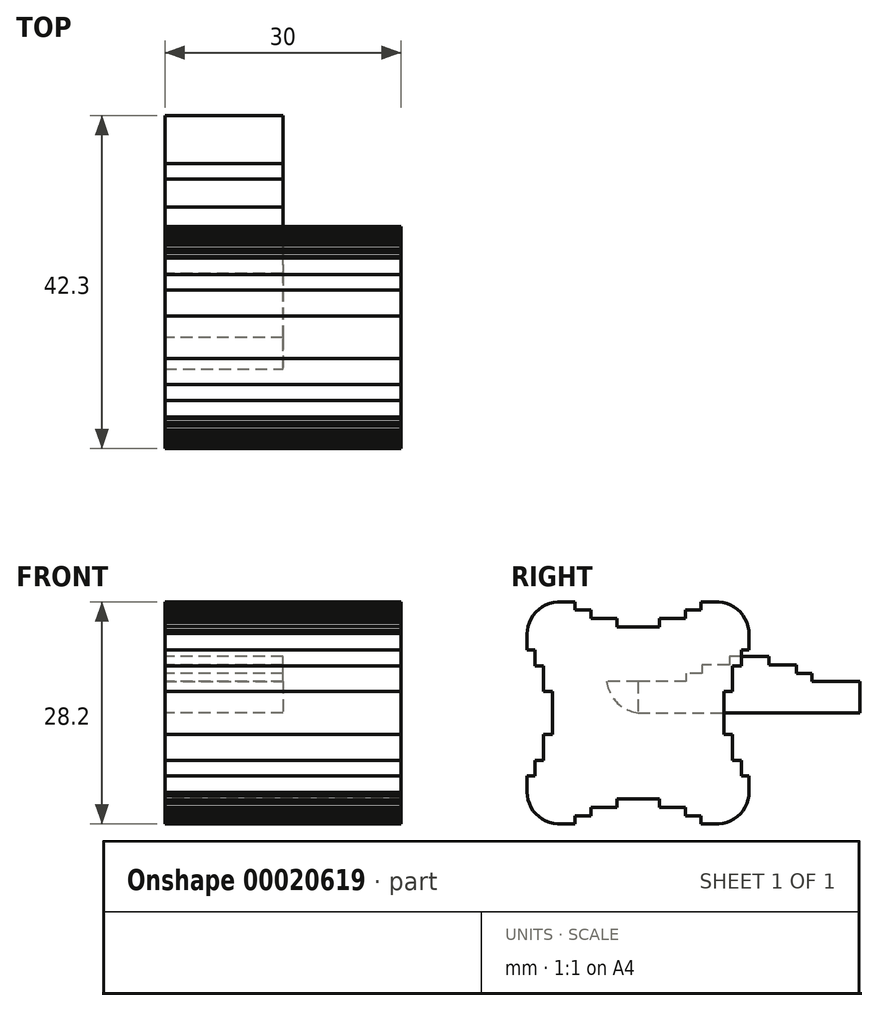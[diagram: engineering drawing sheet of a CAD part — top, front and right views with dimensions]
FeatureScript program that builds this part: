
annotation { "Feature Type Name" : "Feature", "Feature Type Description" : "" }
export const myFeature = defineFeature(function(context is Context, id is Id, definition is map)
    precondition{}
    {
        {
            var Q0;
            Q0=qCreatedBy(makeId("Right.planeOp"),FACE);
            var sketch = newSketch(context, id + "F0", { "sketchPlane" : qUnion([Q0])});
            skLineSegment(sketch, "E0", {"start": v(0, 0) * mm, "end": v(28.2, 0) * mm});
            skLineSegment(sketch, "E1", {"start": v(28.2, 0) * mm, "end": v(28.2, 4) * mm});
            skLineSegment(sketch, "E2", {"start": v(28.2, 4) * mm, "end": v(22.1, 4) * mm});
            skLineSegment(sketch, "E3", {"start": v(22.1, 4) * mm, "end": v(22.1, 5) * mm});
            skLineSegment(sketch, "E4", {"start": v(22.1, 5) * mm, "end": v(20.1, 5) * mm});
            skLineSegment(sketch, "E5", {"start": v(20.1, 5) * mm, "end": v(20.1, 6.1) * mm});
            skLineSegment(sketch, "E6", {"start": v(20.1, 6.1) * mm, "end": v(16.6, 6.1) * mm});
            skLineSegment(sketch, "E7", {"start": v(16.6, 6.1) * mm, "end": v(16.6, 7.2) * mm});
            skLineSegment(sketch, "E8", {"start": v(16.6, 7.2) * mm, "end": v(11.6, 7.2) * mm});
            skLineSegment(sketch, "E9", {"start": v(11.6, 7.2) * mm, "end": v(11.6, 6.1) * mm});
            skLineSegment(sketch, "E10", {"start": v(11.6, 6.1) * mm, "end": v(8.1, 6.1) * mm});
            skLineSegment(sketch, "E11", {"start": v(8.1, 6.1) * mm, "end": v(8.1, 5) * mm});
            skLineSegment(sketch, "E12", {"start": v(8.1, 5) * mm, "end": v(6.1, 5) * mm});
            skLineSegment(sketch, "E13", {"start": v(6.1, 5) * mm, "end": v(6.1, 4) * mm});
            skLineSegment(sketch, "E14", {"start": v(6.1, 4) * mm, "end": v(0, 4) * mm});
            skLineSegment(sketch, "E15", {"start": v(0, 4) * mm, "end": v(0, 0) * mm});
            skSolve(sketch);
        }
        {
            var Q0;
            Q0=qCreatedBy(makeId("Right.planeOp"),FACE);
            var sketch = newSketch(context, id + "F1", { "sketchPlane" : qUnion([Q0])});
            skLineSegment(sketch, "E16", {"start": v(-8, -13.1) * mm, "end": v(-6, -13.1) * mm});
            skLineSegment(sketch, "E17", {"start": v(-6, -13.1) * mm, "end": v(-6, -12) * mm});
            skLineSegment(sketch, "E18", {"start": v(-6, -12) * mm, "end": v(-2.7, -12) * mm});
            skLineSegment(sketch, "E19", {"start": v(-2.7, -12) * mm, "end": v(-2.7, -10.9) * mm});
            skLineSegment(sketch, "E20", {"start": v(-2.7, -10.9) * mm, "end": v(2.7, -10.9) * mm});
            skLineSegment(sketch, "E21", {"start": v(2.7, -10.9) * mm, "end": v(2.7, -12) * mm});
            skLineSegment(sketch, "E22", {"start": v(2.7, -12) * mm, "end": v(6, -12) * mm});
            skLineSegment(sketch, "E23", {"start": v(6, -12) * mm, "end": v(6, -13.1) * mm});
            skLineSegment(sketch, "E24", {"start": v(6, -13.1) * mm, "end": v(8, -13.1) * mm});
            skLineSegment(sketch, "E25", {"start": v(8, -13.1) * mm, "end": v(8, -14.1) * mm});
            skLineSegment(sketch, "E26", {"start": v(8, -14.1) * mm, "end": v(10.1, -14.1) * mm});
            skLineSegment(sketch, "E27", {"start": v(10.1, -14.1) * mm, "end": v(10.1, -14.1) * mm});
            skLineSegment(sketch, "E28", {"start": v(10.1, -14.1) * mm, "end": v(10.26, -14.1) * mm});
            skLineSegment(sketch, "E29", {"start": v(10.26, -14.1) * mm, "end": v(10.77, -14.03) * mm});
            skLineSegment(sketch, "E30", {"start": v(10.77, -14.03) * mm, "end": v(11.27, -13.9) * mm});
            skLineSegment(sketch, "E31", {"start": v(11.27, -13.9) * mm, "end": v(11.75, -13.7) * mm});
            skLineSegment(sketch, "E32", {"start": v(11.75, -13.7) * mm, "end": v(12.2, -13.46) * mm});
            skLineSegment(sketch, "E33", {"start": v(12.2, -13.46) * mm, "end": v(12.61, -13.16) * mm});
            skLineSegment(sketch, "E34", {"start": v(12.61, -13.16) * mm, "end": v(12.99, -12.8) * mm});
            skLineSegment(sketch, "E35", {"start": v(12.99, -12.8) * mm, "end": v(13.32, -12.4) * mm});
            skLineSegment(sketch, "E36", {"start": v(13.32, -12.4) * mm, "end": v(13.6, -11.98) * mm});
            skLineSegment(sketch, "E37", {"start": v(13.6, -11.98) * mm, "end": v(13.81, -11.5) * mm});
            skLineSegment(sketch, "E38", {"start": v(13.81, -11.5) * mm, "end": v(13.97, -11.02) * mm});
            skLineSegment(sketch, "E39", {"start": v(13.97, -11.02) * mm, "end": v(14.07, -10.51) * mm});
            skLineSegment(sketch, "E40", {"start": v(14.07, -10.51) * mm, "end": v(14.1, -10.1) * mm});
            skLineSegment(sketch, "E41", {"start": v(14.1, -10.1) * mm, "end": v(14.1, -10.1) * mm});
            skLineSegment(sketch, "E42", {"start": v(14.1, -10.1) * mm, "end": v(14.1, -8) * mm});
            skLineSegment(sketch, "E43", {"start": v(14.1, -8) * mm, "end": v(13.1, -8) * mm});
            skLineSegment(sketch, "E44", {"start": v(13.1, -8) * mm, "end": v(13.1, -6) * mm});
            skLineSegment(sketch, "E45", {"start": v(13.1, -6) * mm, "end": v(12, -6) * mm});
            skLineSegment(sketch, "E46", {"start": v(12, -6) * mm, "end": v(12, -2.75) * mm});
            skLineSegment(sketch, "E47", {"start": v(12, -2.75) * mm, "end": v(10.9, -2.75) * mm});
            skLineSegment(sketch, "E48", {"start": v(10.9, -2.75) * mm, "end": v(10.9, 2.75) * mm});
            skLineSegment(sketch, "E49", {"start": v(10.9, 2.75) * mm, "end": v(12, 2.75) * mm});
            skLineSegment(sketch, "E50", {"start": v(12, 2.75) * mm, "end": v(12, 6) * mm});
            skLineSegment(sketch, "E51", {"start": v(12, 6) * mm, "end": v(13.1, 6) * mm});
            skLineSegment(sketch, "E52", {"start": v(13.1, 6) * mm, "end": v(13.1, 8) * mm});
            skLineSegment(sketch, "E53", {"start": v(13.1, 8) * mm, "end": v(14.1, 8) * mm});
            skLineSegment(sketch, "E54", {"start": v(14.1, 8) * mm, "end": v(14.1, 10.1) * mm});
            skLineSegment(sketch, "E55", {"start": v(14.1, 10.1) * mm, "end": v(14.1, 10.1) * mm});
            skLineSegment(sketch, "E56", {"start": v(14.1, 10.1) * mm, "end": v(14.07, 10.51) * mm});
            skLineSegment(sketch, "E57", {"start": v(14.07, 10.51) * mm, "end": v(13.97, 11.02) * mm});
            skLineSegment(sketch, "E58", {"start": v(13.97, 11.02) * mm, "end": v(13.81, 11.5) * mm});
            skLineSegment(sketch, "E59", {"start": v(13.81, 11.5) * mm, "end": v(13.6, 11.98) * mm});
            skLineSegment(sketch, "E60", {"start": v(13.6, 11.98) * mm, "end": v(13.32, 12.4) * mm});
            skLineSegment(sketch, "E61", {"start": v(13.32, 12.4) * mm, "end": v(12.99, 12.8) * mm});
            skLineSegment(sketch, "E62", {"start": v(12.99, 12.8) * mm, "end": v(12.61, 13.16) * mm});
            skLineSegment(sketch, "E63", {"start": v(12.61, 13.16) * mm, "end": v(12.2, 13.46) * mm});
            skLineSegment(sketch, "E64", {"start": v(12.2, 13.46) * mm, "end": v(11.75, 13.7) * mm});
            skLineSegment(sketch, "E65", {"start": v(11.75, 13.7) * mm, "end": v(11.27, 13.9) * mm});
            skLineSegment(sketch, "E66", {"start": v(11.27, 13.9) * mm, "end": v(10.77, 14.03) * mm});
            skLineSegment(sketch, "E67", {"start": v(10.77, 14.03) * mm, "end": v(10.26, 14.1) * mm});
            skLineSegment(sketch, "E68", {"start": v(10.26, 14.1) * mm, "end": v(10.1, 14.1) * mm});
            skLineSegment(sketch, "E69", {"start": v(10.1, 14.1) * mm, "end": v(10.1, 14.1) * mm});
            skLineSegment(sketch, "E70", {"start": v(10.1, 14.1) * mm, "end": v(8, 14.1) * mm});
            skLineSegment(sketch, "E71", {"start": v(8, 14.1) * mm, "end": v(8, 13.1) * mm});
            skLineSegment(sketch, "E72", {"start": v(8, 13.1) * mm, "end": v(6, 13.1) * mm});
            skLineSegment(sketch, "E73", {"start": v(6, 13.1) * mm, "end": v(6, 12) * mm});
            skLineSegment(sketch, "E74", {"start": v(6, 12) * mm, "end": v(2.7, 12) * mm});
            skLineSegment(sketch, "E75", {"start": v(2.7, 12) * mm, "end": v(2.7, 10.9) * mm});
            skLineSegment(sketch, "E76", {"start": v(2.7, 10.9) * mm, "end": v(-2.7, 10.9) * mm});
            skLineSegment(sketch, "E77", {"start": v(-2.7, 10.9) * mm, "end": v(-2.7, 12) * mm});
            skLineSegment(sketch, "E78", {"start": v(-2.7, 12) * mm, "end": v(-6, 12) * mm});
            skLineSegment(sketch, "E79", {"start": v(-6, 12) * mm, "end": v(-6, 13.1) * mm});
            skLineSegment(sketch, "E80", {"start": v(-6, 13.1) * mm, "end": v(-8, 13.1) * mm});
            skLineSegment(sketch, "E81", {"start": v(-8, 13.1) * mm, "end": v(-8, 14.1) * mm});
            skLineSegment(sketch, "E82", {"start": v(-8, 14.1) * mm, "end": v(-10.1, 14.1) * mm});
            skLineSegment(sketch, "E83", {"start": v(-10.1, 14.1) * mm, "end": v(-10.1, 14.1) * mm});
            skLineSegment(sketch, "E84", {"start": v(-10.1, 14.1) * mm, "end": v(-10.26, 14.1) * mm});
            skLineSegment(sketch, "E85", {"start": v(-10.26, 14.1) * mm, "end": v(-10.77, 14.03) * mm});
            skLineSegment(sketch, "E86", {"start": v(-10.77, 14.03) * mm, "end": v(-11.27, 13.9) * mm});
            skLineSegment(sketch, "E87", {"start": v(-11.27, 13.9) * mm, "end": v(-11.75, 13.7) * mm});
            skLineSegment(sketch, "E88", {"start": v(-11.75, 13.7) * mm, "end": v(-12.2, 13.46) * mm});
            skLineSegment(sketch, "E89", {"start": v(-12.2, 13.46) * mm, "end": v(-12.61, 13.16) * mm});
            skLineSegment(sketch, "E90", {"start": v(-12.61, 13.16) * mm, "end": v(-12.99, 12.8) * mm});
            skLineSegment(sketch, "E91", {"start": v(-12.99, 12.8) * mm, "end": v(-13.32, 12.4) * mm});
            skLineSegment(sketch, "E92", {"start": v(-13.32, 12.4) * mm, "end": v(-13.6, 11.98) * mm});
            skLineSegment(sketch, "E93", {"start": v(-13.6, 11.98) * mm, "end": v(-13.81, 11.5) * mm});
            skLineSegment(sketch, "E94", {"start": v(-13.81, 11.5) * mm, "end": v(-13.97, 11.02) * mm});
            skLineSegment(sketch, "E95", {"start": v(-13.97, 11.02) * mm, "end": v(-14.07, 10.51) * mm});
            skLineSegment(sketch, "E96", {"start": v(-14.07, 10.51) * mm, "end": v(-14.1, 10.1) * mm});
            skLineSegment(sketch, "E97", {"start": v(-14.1, 10.1) * mm, "end": v(-14.1, 10.1) * mm});
            skLineSegment(sketch, "E98", {"start": v(-14.1, 10.1) * mm, "end": v(-14.1, 8) * mm});
            skLineSegment(sketch, "E99", {"start": v(-14.1, 8) * mm, "end": v(-13.1, 8) * mm});
            skLineSegment(sketch, "E100", {"start": v(-13.1, 8) * mm, "end": v(-13.1, 6) * mm});
            skLineSegment(sketch, "E101", {"start": v(-13.1, 6) * mm, "end": v(-12, 6) * mm});
            skLineSegment(sketch, "E102", {"start": v(-12, 6) * mm, "end": v(-12, 2.75) * mm});
            skLineSegment(sketch, "E103", {"start": v(-12, 2.75) * mm, "end": v(-10.9, 2.75) * mm});
            skLineSegment(sketch, "E104", {"start": v(-10.9, 2.75) * mm, "end": v(-10.9, -2.75) * mm});
            skLineSegment(sketch, "E105", {"start": v(-10.9, -2.75) * mm, "end": v(-12, -2.75) * mm});
            skLineSegment(sketch, "E106", {"start": v(-12, -2.75) * mm, "end": v(-12, -6) * mm});
            skLineSegment(sketch, "E107", {"start": v(-12, -6) * mm, "end": v(-13.1, -6) * mm});
            skLineSegment(sketch, "E108", {"start": v(-13.1, -6) * mm, "end": v(-13.1, -8) * mm});
            skLineSegment(sketch, "E109", {"start": v(-13.1, -8) * mm, "end": v(-14.1, -8) * mm});
            skLineSegment(sketch, "E110", {"start": v(-14.1, -8) * mm, "end": v(-14.1, -10.1) * mm});
            skLineSegment(sketch, "E111", {"start": v(-14.1, -10.1) * mm, "end": v(-14.1, -10.1) * mm});
            skLineSegment(sketch, "E112", {"start": v(-14.1, -10.1) * mm, "end": v(-14.07, -10.51) * mm});
            skLineSegment(sketch, "E113", {"start": v(-14.07, -10.51) * mm, "end": v(-13.97, -11.02) * mm});
            skLineSegment(sketch, "E114", {"start": v(-13.97, -11.02) * mm, "end": v(-13.81, -11.5) * mm});
            skLineSegment(sketch, "E115", {"start": v(-13.81, -11.5) * mm, "end": v(-13.6, -11.98) * mm});
            skLineSegment(sketch, "E116", {"start": v(-13.6, -11.98) * mm, "end": v(-13.32, -12.4) * mm});
            skLineSegment(sketch, "E117", {"start": v(-13.32, -12.4) * mm, "end": v(-12.99, -12.8) * mm});
            skLineSegment(sketch, "E118", {"start": v(-12.99, -12.8) * mm, "end": v(-12.61, -13.16) * mm});
            skLineSegment(sketch, "E119", {"start": v(-12.61, -13.16) * mm, "end": v(-12.2, -13.46) * mm});
            skLineSegment(sketch, "E120", {"start": v(-12.2, -13.46) * mm, "end": v(-11.75, -13.7) * mm});
            skLineSegment(sketch, "E121", {"start": v(-11.75, -13.7) * mm, "end": v(-11.27, -13.9) * mm});
            skLineSegment(sketch, "E122", {"start": v(-11.27, -13.9) * mm, "end": v(-10.77, -14.03) * mm});
            skLineSegment(sketch, "E123", {"start": v(-10.77, -14.03) * mm, "end": v(-10.26, -14.1) * mm});
            skLineSegment(sketch, "E124", {"start": v(-10.26, -14.1) * mm, "end": v(-10.1, -14.1) * mm});
            skLineSegment(sketch, "E125", {"start": v(-10.1, -14.1) * mm, "end": v(-10.1, -14.1) * mm});
            skLineSegment(sketch, "E126", {"start": v(-10.1, -14.1) * mm, "end": v(-8, -14.1) * mm});
            skLineSegment(sketch, "E127", {"start": v(-8, -14.1) * mm, "end": v(-8, -13.1) * mm});
            skSolve(sketch);
        }
        {
            var Q0;
            Q0 = qSketchRegion(id + "F1", true);
            extrude(context, id + "F2", {"entities" : qUnion([Q0]), "depth" : 30 * mm});
        }
        {
            var Q0;
            Q0=qCreatedBy(makeId("Right.planeOp"),FACE);
            var sketch = newSketch(context, id + "F3", { "sketchPlane" : qUnion([Q0])});
            skLineSegment(sketch, "E128.bottom", {"start": v(0, 0) * mm, "end": v(-4, 0) * mm});
            skLineSegment(sketch, "E128.top", {"start": v(0, 4) * mm, "end": v(-4, 4) * mm});
            skLineSegment(sketch, "E128.left", {"start": v(0, 0) * mm, "end": v(0, 4) * mm});
            skLineSegment(sketch, "E128.right", {"start": v(-4, 0) * mm, "end": v(-4, 4) * mm});
            skSolve(sketch);
        }
        {
            var Q0;
            Q0 = qSketchRegion(id + "F0", true);
            var Q1;
            Q1 = qSketchRegion(id + "F3", true);
            extrude(context, id + "F4", {"entities" : qUnion([Q0, Q1]), "depth" : 15 * mm});
        }
        {
            var Q0;
            Q0=makeQuery(id+"F4.opExtrude","SWEPT_EDGE",EDGE,{"disambiguationData":[OSD([sQuery(id+"F3.wireOp",EDGE,"E128.bottom"),sQuery(id+"F3.wireOp",EDGE,"E128.right")])]});
            fillet(context, id + "F5", {"entities" : qUnion([Q0]), "radius" : 5 * mm, "rho" : 0.5, "crossSection" : FilletCrossSection.CONIC, "allowEdgeOverflow" : false});
        }
    });
